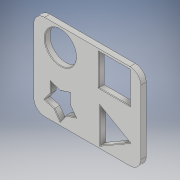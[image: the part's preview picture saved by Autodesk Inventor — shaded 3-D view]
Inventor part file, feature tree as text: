
AUTODESK INVENTOR PART (.ipt)
format: ipt  version: 2017 (Build 210142000, 142)  size: 229,888 bytes
history: native  units: in
note: dims shown in document units (in); Inventor stores cm internally (conversion verified against a paired STEP export)
features: extrude x1, fillet x1, shell x1, sketch x1
ambient origin geometry x8: Origin, YZ Plane, XZ Plane, XY Plane, X Axis, Y Axis, Z Axis, Center Point
bodies: Solid1 (feature_tree)
feature tree (4):
  extrude  "Extrusion1"  Depth=1.59in
  fillet  "Fillet1"  Radius=0.2in
  shell  "Shell1"  Thickness=0.58in
  sketch  "Sketch1"  dims[d0=1.98in d1=1.59in d2=0.2in d3=0.58in d5=0.05in d7=0.2in d8=0.58in d9=0.58in d10=0.05in d11=0.2in d12=0.638in d13=0.638in d14=0.638in d15=60.0deg d16=0.2in d17=0.05in d18=0.605in d19=0.1778in d20=0.1778in d21=0.187in d22=0.1513in d23=0.4947in d24=0.187in d25=0.4947in d26=0.1513in d27=0.4947in d28=0.4947in d29=0.4947in d30=0.1778in d31=1.0669in d32=0.2461in d33=0.2916in d34=0.2528in d35=0.3031in d36=2.912in d37=0.1in d38=0.0in d39=0.01in d40=0.01in]
